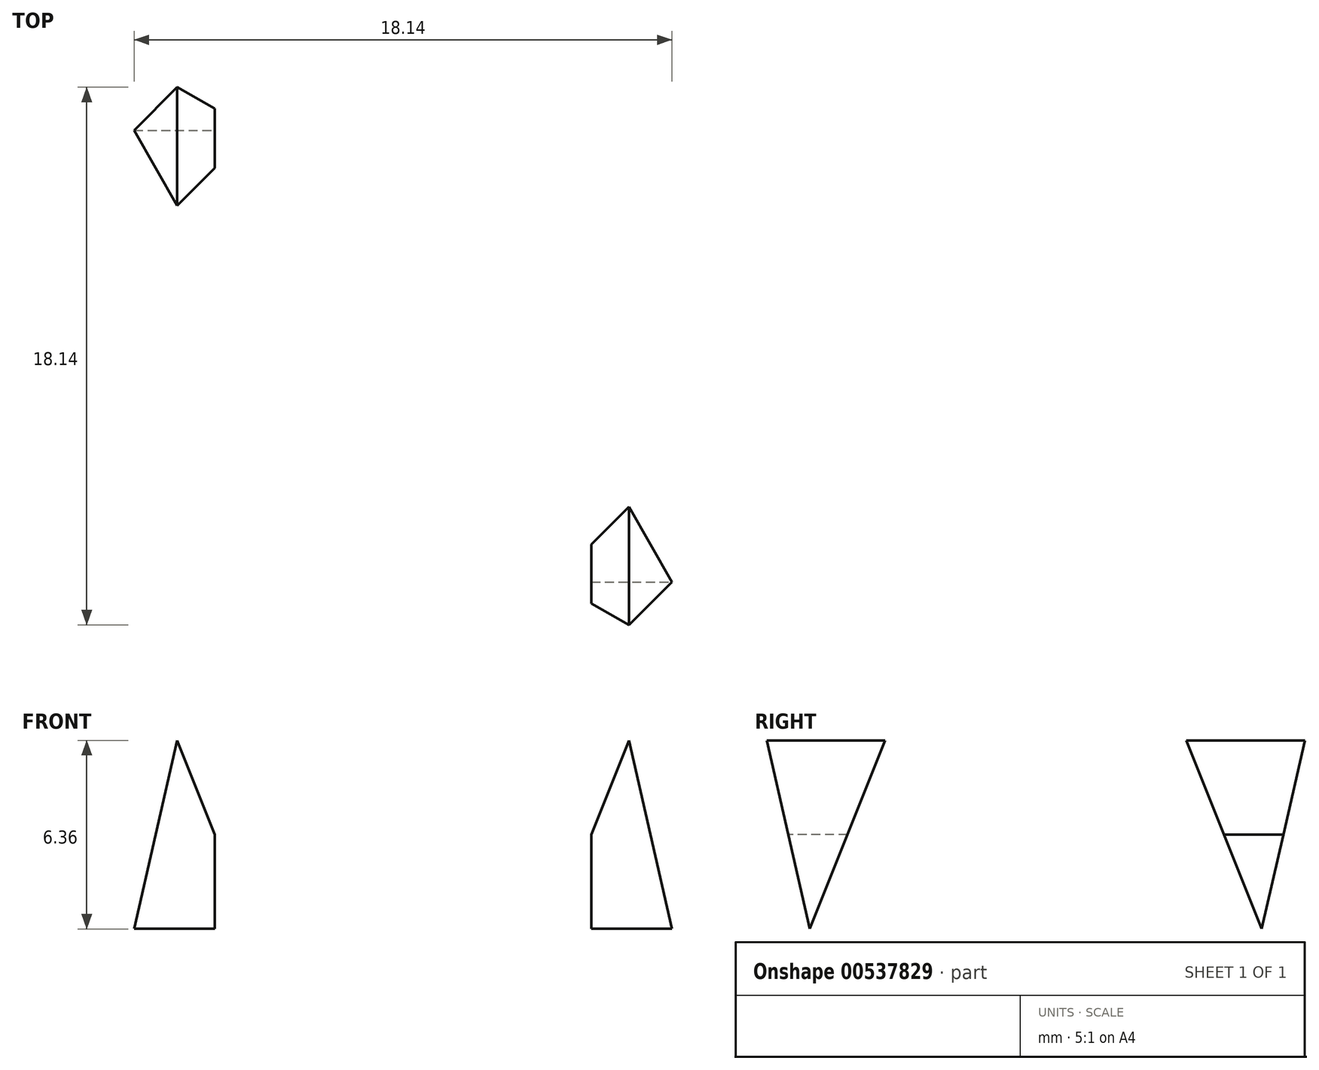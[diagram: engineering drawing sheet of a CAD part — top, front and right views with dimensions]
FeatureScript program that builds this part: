
annotation { "Feature Type Name" : "Feature", "Feature Type Description" : "" }
export const myFeature = defineFeature(function(context is Context, id is Id, definition is map)
    precondition{}
    {
        {
            var Q0;
            Q0=qCreatedBy(makeId("Front.planeOp"),FACE);
            var sketch = newSketch(context, id + "F0", { "sketchPlane" : qUnion([Q0])});
            skLineSegment(sketch, "E0", {"start": v(0, 0) * mm, "end": v(0, 38.1) * mm});
            skLineSegment(sketch, "E1", {"start": v(0, 38.1) * mm, "end": v(38.1, 38.1) * mm});
            skLineSegment(sketch, "E2", {"start": v(38.1, 38.1) * mm, "end": v(38.1, 0) * mm});
            skLineSegment(sketch, "E3", {"start": v(38.1, 0) * mm, "end": v(0, 0) * mm});
            skSolve(sketch);
        }
        {
            var Q0;
            Q0 = qSketchRegion(id + "F0", true);
            extrude(context, id + "F1", {"entities" : qUnion([Q0]), "depth" : 38.1 * mm, "offsetDistance" : 25.4 * mm});
        }
        {
            var Q0;
            Q0=qCreatedBy(makeId("Front.planeOp"),FACE);
            cPlane(context, id + "F2", {"entities" : qUnion([Q0]), "cplaneType" : CPlaneType.OFFSET, "offset" : 38.1 * mm, "width" : 152.4 * mm, "height" : 152.4 * mm});
        }
        {
            var Q0;
            Q0=qCreatedBy(makeId("Right.planeOp"),FACE);
            cPlane(context, id + "F3", {"entities" : qUnion([Q0]), "cplaneType" : CPlaneType.OFFSET, "offset" : 38.1 * mm, "width" : 152.4 * mm, "height" : 152.4 * mm});
        }
        {
            var Q0;
            Q0=qCreatedBy(makeId("Top.planeOp"),FACE);
            cPlane(context, id + "F4", {"entities" : qUnion([Q0]), "cplaneType" : CPlaneType.OFFSET, "offset" : 38.1 * mm, "width" : 152.4 * mm, "height" : 152.4 * mm});
        }
        {
            var Q0;
            Q0=qCreatedBy(id+"F3.planeOp",FACE);
            var sketch = newSketch(context, id + "F5", { "sketchPlane" : qUnion([Q0])});
            skLineSegment(sketch, "E4", {"start": v(0, 0) * mm, "end": v(0, 38.1) * mm});
            skLineSegment(sketch, "E5", {"start": v(0, 38.1) * mm, "end": v(-38.1, 38.1) * mm});
            skLineSegment(sketch, "E6", {"start": v(-38.1, 38.1) * mm, "end": v(-38.1, 0) * mm});
            skLineSegment(sketch, "E7", {"start": v(-38.1, 0) * mm, "end": v(0, 0) * mm});
            skLineSegment(sketch, "E8", {"start": v(-38.1, 38.1) * mm, "end": v(-31.75, 0) * mm});
            skLineSegment(sketch, "E9", {"start": v(-31.75, 0) * mm, "end": v(-25.4, 0) * mm});
            skLineSegment(sketch, "E10", {"start": v(-25.4, 0) * mm, "end": v(-19.05, 15.88) * mm});
            skLineSegment(sketch, "E11", {"start": v(-19.05, 15.88) * mm, "end": v(-12.7, 0) * mm});
            skLineSegment(sketch, "E12", {"start": v(-12.7, 0) * mm, "end": v(-6.35, 0) * mm});
            skLineSegment(sketch, "E13", {"start": v(-6.35, 0) * mm, "end": v(0, 38.1) * mm});
            skLineSegment(sketch, "E14", {"start": v(-38.1, 38.1) * mm, "end": v(-31.75, 38.1) * mm});
            skLineSegment(sketch, "E15", {"start": v(-31.75, 38.1) * mm, "end": v(-26.67, 15.87) * mm});
            skLineSegment(sketch, "E16", {"start": v(-26.67, 15.87) * mm, "end": v(-21.59, 28.58) * mm});
            skPoint(sketch, "E16.endSnap0", {"position": v(-34.45, 19.05) * mm});
            skLineSegment(sketch, "E17", {"start": v(-21.59, 28.58) * mm, "end": v(-16.5, 28.58) * mm});
            skLineSegment(sketch, "E18", {"start": v(-16.5, 28.58) * mm, "end": v(-11.43, 15.88) * mm});
            skLineSegment(sketch, "E19", {"start": v(0, 38.1) * mm, "end": v(-6.35, 38.1) * mm});
            skLineSegment(sketch, "E20", {"start": v(-6.35, 38.1) * mm, "end": v(-11.43, 15.87) * mm});
            skSolve(sketch);
        }
        {
            var Q0;
            {var subQ0=sQuery(id+"F5.wireOp",EDGE,"E6");Q0=makeQuery(id+"F5.imprint","IMPRINT",FACE,{"disambiguationData":[TD([[makeQuery(id+"F5.imprint","IMPRINT",EDGE,{"derivedFrom":subQ0}),1.0]])]});}
            var Q1;
            Q1=makeQuery(id+"F5.imprint","IMPRINT",FACE,{"disambiguationData":[TD([[makeQuery(id+"F5.imprint","IMPRINT",EDGE,{"derivedFrom":sQuery(id+"F5.wireOp",EDGE,"E5")}),1.0]])]});
            var Q2;
            {var subQ0=sQuery(id+"F5.wireOp",EDGE,"E4");Q2=makeQuery(id+"F5.imprint","IMPRINT",FACE,{"disambiguationData":[TD([[makeQuery(id+"F5.imprint","IMPRINT",EDGE,{"derivedFrom":subQ0}),1.0]])]});}
            var Q3;
            {var subQ0=sQuery(id+"F5.wireOp",EDGE,"E10");Q3=makeQuery(id+"F5.imprint","IMPRINT",FACE,{"disambiguationData":[TD([[makeQuery(id+"F5.imprint","IMPRINT",EDGE,{"derivedFrom":subQ0}),-1.0]])]});}
            extrude(context, id + "F6", {"entities" : qUnion([Q0, Q1, Q2, Q3]), "operationType" : NewBodyOperationType.REMOVE, "oppositeDirection" : true, "depth" : 38.1 * mm, "offsetDistance" : 25.4 * mm});
        }
        {
            var Q0;
            Q0=qCreatedBy(id+"F2.planeOp",FACE);
            var sketch = newSketch(context, id + "F7", { "sketchPlane" : qUnion([Q0])});
            skLineSegment(sketch, "E21", {"start": v(0, 0) * mm, "end": v(0, 38.1) * mm});
            skLineSegment(sketch, "E22", {"start": v(0, 38.1) * mm, "end": v(38.1, 38.1) * mm});
            skLineSegment(sketch, "E23", {"start": v(38.1, 0) * mm, "end": v(0, 0) * mm});
            skLineSegment(sketch, "E24", {"start": v(0, 0) * mm, "end": v(6.35, 38.1) * mm});
            skLineSegment(sketch, "E25", {"start": v(6.35, 38.1) * mm, "end": v(12.7, 38.1) * mm});
            skLineSegment(sketch, "E26", {"start": v(12.7, 38.1) * mm, "end": v(19.05, 22.23) * mm});
            skLineSegment(sketch, "E27", {"start": v(19.05, 22.23) * mm, "end": v(25.4, 38.1) * mm});
            skLineSegment(sketch, "E28", {"start": v(25.4, 38.1) * mm, "end": v(31.75, 38.1) * mm});
            skLineSegment(sketch, "E29", {"start": v(31.75, 38.1) * mm, "end": v(38.1, 0) * mm});
            skLineSegment(sketch, "E30", {"start": v(31.75, 0) * mm, "end": v(38.1, 0) * mm});
            skLineSegment(sketch, "E31", {"start": v(31.75, 0) * mm, "end": v(26.67, 22.23) * mm});
            skLineSegment(sketch, "E32", {"start": v(26.67, 22.23) * mm, "end": v(21.59, 9.53) * mm});
            skLineSegment(sketch, "E33", {"start": v(21.59, 9.53) * mm, "end": v(16.5, 9.53) * mm});
            skLineSegment(sketch, "E34", {"start": v(16.5, 9.52) * mm, "end": v(11.43, 22.23) * mm});
            skLineSegment(sketch, "E35", {"start": v(11.43, 22.23) * mm, "end": v(6.35, 0) * mm});
            skLineSegment(sketch, "E36", {"start": v(6.35, 0) * mm, "end": v(0, 0) * mm});
            skLineSegment(sketch, "E37", {"start": v(38.1, 38.1) * mm, "end": v(38.1, 0) * mm});
            skSolve(sketch);
        }
        {
            var Q0;
            Q0=makeQuery(id+"F7.imprint","IMPRINT",FACE,{"disambiguationData":[TD([[makeQuery(id+"F7.imprint","IMPRINT",EDGE,{"derivedFrom":sQuery(id+"F7.wireOp",EDGE,"E23")}),-1.0]])]});
            var Q1;
            {var subQ0=sQuery(id+"F7.wireOp",EDGE,"E26");Q1=makeQuery(id+"F7.imprint","IMPRINT",FACE,{"disambiguationData":[TD([[makeQuery(id+"F7.imprint","IMPRINT",EDGE,{"derivedFrom":subQ0}),1.0]])]});}
            var Q2;
            {var subQ0=sQuery(id+"F7.wireOp",EDGE,"E21");Q2=makeQuery(id+"F7.imprint","IMPRINT",FACE,{"disambiguationData":[TD([[makeQuery(id+"F7.imprint","IMPRINT",EDGE,{"derivedFrom":subQ0}),-1.0]])]});}
            var Q3;
            {var subQ2=sQuery(id+"F7.wireOp",EDGE,"E29");Q3=makeQuery(id+"F7.imprint","IMPRINT",FACE,{"disambiguationData":[TD([[makeQuery(id+"F7.imprint","IMPRINT",EDGE,{"derivedFrom":subQ2}),1.0]])]});}
            extrude(context, id + "F8", {"entities" : qUnion([Q0, Q1, Q2, Q3]), "operationType" : NewBodyOperationType.REMOVE, "oppositeDirection" : true, "depth" : 38.1 * mm, "offsetDistance" : 25.4 * mm});
        }
        {
            var Q0;
            Q0=qCreatedBy(id+"F4.planeOp",FACE);
            var sketch = newSketch(context, id + "F9", { "sketchPlane" : qUnion([Q0])});
            skLineSegment(sketch, "E38", {"start": v(0, 0) * mm, "end": v(0, -38.1) * mm});
            skLineSegment(sketch, "E39", {"start": v(0, -38.1) * mm, "end": v(38.1, -38.1) * mm});
            skLineSegment(sketch, "E40", {"start": v(38.1, -38.1) * mm, "end": v(38.1, 0) * mm});
            skLineSegment(sketch, "E41", {"start": v(38.1, 0) * mm, "end": v(0, 0) * mm});
            skLineSegment(sketch, "E42", {"start": v(38.1, -7.62) * mm, "end": v(12.7, -7.62) * mm});
            skLineSegment(sketch, "E43", {"start": v(12.7, -7.62) * mm, "end": v(12.7, -15.24) * mm});
            skLineSegment(sketch, "E44", {"start": v(12.7, -15.24) * mm, "end": v(38.1, -15.24) * mm});
            skLineSegment(sketch, "E45", {"start": v(0, -22.86) * mm, "end": v(25.4, -22.86) * mm});
            skLineSegment(sketch, "E46", {"start": v(25.4, -22.86) * mm, "end": v(25.4, -30.48) * mm});
            skLineSegment(sketch, "E47", {"start": v(25.4, -30.48) * mm, "end": v(0, -30.48) * mm});
            skSolve(sketch);
        }
        {
            var Q0;
            {var subQ0=sQuery(id+"F9.wireOp",EDGE,"E42");Q0=makeQuery(id+"F9.imprint","IMPRINT",FACE,{"disambiguationData":[TD([[makeQuery(id+"F9.imprint","IMPRINT",EDGE,{"derivedFrom":subQ0}),1.0]])]});}
            var Q1;
            {var subQ0=sQuery(id+"F9.wireOp",EDGE,"E45");Q1=makeQuery(id+"F9.imprint","IMPRINT",FACE,{"disambiguationData":[TD([[makeQuery(id+"F9.imprint","IMPRINT",EDGE,{"derivedFrom":subQ0}),-1.0]])]});}
            extrude(context, id + "F10", {"entities" : qUnion([Q0, Q1]), "operationType" : NewBodyOperationType.REMOVE, "oppositeDirection" : true, "depth" : 38.1 * mm, "offsetDistance" : 25.4 * mm});
        }
    });
